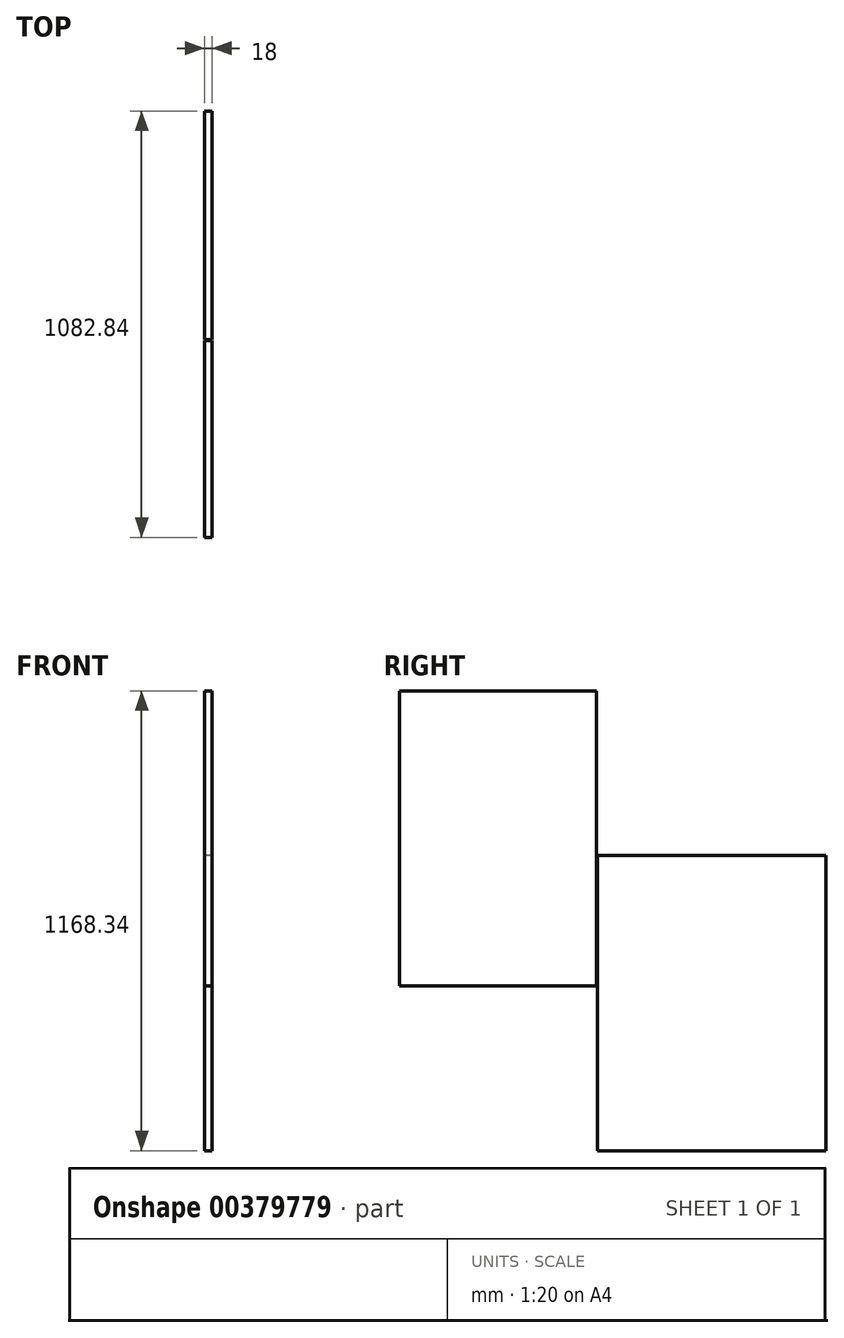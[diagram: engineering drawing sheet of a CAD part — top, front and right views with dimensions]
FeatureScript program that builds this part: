
annotation { "Feature Type Name" : "Feature", "Feature Type Description" : "" }
export const myFeature = defineFeature(function(context is Context, id is Id, definition is map)
    precondition{}
    {
        {
            var Q0;
            Q0=qCreatedBy(makeId("Right.planeOp"),FACE);
            var sketch = newSketch(context, id + "F0", { "sketchPlane" : qUnion([Q0])});
            skLineSegment(sketch, "E0.bottom", {"start": v(-300.67, 437.5) * mm, "end": v(199.33, 437.5) * mm});
            skLineSegment(sketch, "E0.top", {"start": v(-300.67, -312.5) * mm, "end": v(199.33, -312.5) * mm});
            skLineSegment(sketch, "E0.left", {"start": v(-300.67, 437.5) * mm, "end": v(-300.67, -312.5) * mm});
            skLineSegment(sketch, "E0.right", {"start": v(199.33, 437.5) * mm, "end": v(199.33, -312.5) * mm});
            skSolve(sketch);
        }
        {
            var Q0;
            Q0=qSketchRegion(id+"F0",true);
            extrude(context, id + "F1", {"entities" : qUnion([Q0]), "depth" : 18 * mm});
        }
        {
            var Q0;
            Q0=qCreatedBy(makeId("Right.planeOp"),FACE);
            var sketch = newSketch(context, id + "F2", { "sketchPlane" : qUnion([Q0])});
            skLineSegment(sketch, "E1.bottom", {"start": v(782.17, 19.15) * mm, "end": v(202.17, 19.15) * mm});
            skLineSegment(sketch, "E1.top", {"start": v(782.17, -730.85) * mm, "end": v(202.17, -730.85) * mm});
            skLineSegment(sketch, "E1.left", {"start": v(782.17, 19.15) * mm, "end": v(782.17, -730.85) * mm});
            skLineSegment(sketch, "E1.right", {"start": v(202.17, 19.15) * mm, "end": v(202.17, -730.85) * mm});
            skSolve(sketch);
        }
        {
            var Q0;
            Q0=makeQuery(id+"F2.imprint","IMPRINT",FACE,{"disambiguationData":[TD([[makeQuery(id+"F2.imprint","IMPRINT",EDGE,{"derivedFrom":sQuery(id+"F2.wireOp",EDGE,"E1.bottom")}),1.0]])]});
            extrude(context, id + "F3", {"entities" : qUnion([Q0]), "depth" : 18 * mm});
        }
    });
